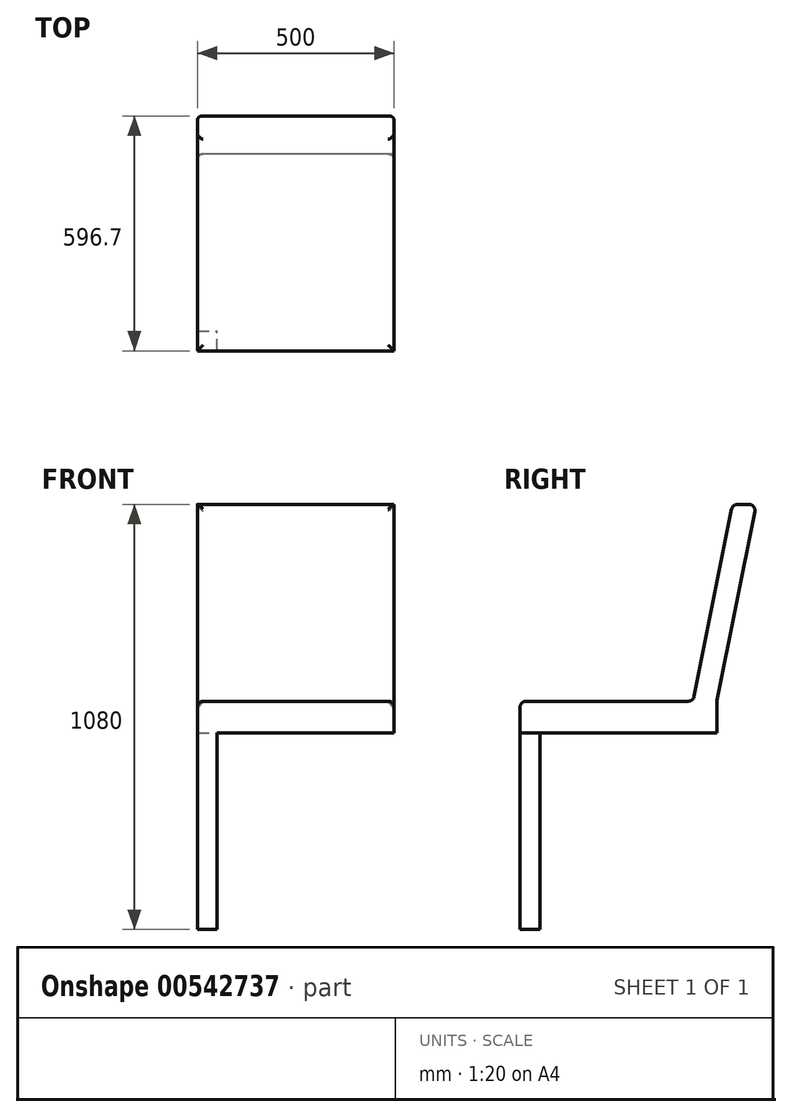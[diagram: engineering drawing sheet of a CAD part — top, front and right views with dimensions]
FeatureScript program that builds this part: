
annotation { "Feature Type Name" : "Feature", "Feature Type Description" : "" }
export const myFeature = defineFeature(function(context is Context, id is Id, definition is map)
    precondition{}
    {
        {
            var Q0;
            Q0=qCreatedBy(makeId("Top.planeOp"),FACE);
            var sketch = newSketch(context, id + "F0", { "sketchPlane" : qUnion([Q0])});
            skLineSegment(sketch, "E0.bottom", {"start": v(250, 250) * mm, "end": v(-250, 250) * mm});
            skLineSegment(sketch, "E0.top", {"start": v(250, -250) * mm, "end": v(-250, -250) * mm});
            skLineSegment(sketch, "E0.left", {"start": v(250, 250) * mm, "end": v(250, -250) * mm});
            skLineSegment(sketch, "E0.right", {"start": v(-250, 250) * mm, "end": v(-250, -250) * mm});
            skPoint(sketch, "E0.middle", {"position": v(0, 0) * mm});
            skSolve(sketch);
        }
        {
            var Q0;
            Q0 = qSketchRegion(id + "F0", true);
            extrude(context, id + "F1", {"entities" : qUnion([Q0]), "depth" : 80 * mm, "offsetDistance" : 25 * mm});
        }
        {
            var Q0;
            Q0=makeQuery(id+"F1.opExtrude","CAP_FACE",FACE,{"disambiguationData":[OSD([sQuery(id+"F0.wireOp",EDGE,"E0.bottom"),sQuery(id+"F0.wireOp",EDGE,"E0.top"),sQuery(id+"F0.wireOp",EDGE,"E0.left"),sQuery(id+"F0.wireOp",EDGE,"E0.right")])],"isStart":true});
            var sketch = newSketch(context, id + "F2", { "sketchPlane" : qUnion([Q0])});
            skLineSegment(sketch, "E1.bottom", {"start": v(-250, 250) * mm, "end": v(-200, 250) * mm});
            skLineSegment(sketch, "E1.top", {"start": v(-250, 200) * mm, "end": v(-200, 200) * mm});
            skLineSegment(sketch, "E1.left", {"start": v(-250, 250) * mm, "end": v(-250, 200) * mm});
            skLineSegment(sketch, "E1.right", {"start": v(-200, 250) * mm, "end": v(-200, 200) * mm});
            skSolve(sketch);
        }
        {
            var Q0;
            Q0 = qSketchRegion(id + "F2", true);
            extrude(context, id + "F3", {"entities" : qUnion([Q0]), "operationType" : NewBodyOperationType.ADD, "depth" : 500 * mm, "offsetDistance" : 25 * mm});
        }
        {
            var Q0;
            Q0=qCreatedBy(makeId("Front.planeOp"),FACE);
            var sketch = newSketch(context, id + "F4", { "sketchPlane" : qUnion([Q0])});
            skLineSegment(sketch, "E2", {"start": v(0, 0) * mm, "end": v(0, -54.17) * mm});
            skSolve(sketch);
        }
        {
            var Q0;
            Q0=qCreatedBy(makeId("Right.planeOp"),FACE);
            var sketch = newSketch(context, id + "F5", { "sketchPlane" : qUnion([Q0])});
            skLineSegment(sketch, "E3", {"start": v(190, 80) * mm, "end": v(290, 580) * mm});
            skLineSegment(sketch, "E4", {"start": v(290, 580) * mm, "end": v(350, 580) * mm});
            skLineSegment(sketch, "E5", {"start": v(350, 580) * mm, "end": v(250, 80) * mm});
            skLineSegment(sketch, "E6", {"start": v(250, 80) * mm, "end": v(190, 80) * mm});
            skSolve(sketch);
        }
        {
            var Q0;
            Q0 = qSketchRegion(id + "F5", true);
            extrude(context, id + "F6", {"entities" : qUnion([Q0]), "operationType" : NewBodyOperationType.ADD, "depth" : 500 * mm, "offsetDistance" : 25 * mm, "symmetric" : true});
        }
        {
            var Q0;
            Q0=makeQuery(id+"F1.opExtrude","CAP_FACE",FACE,{"disambiguationData":[OSD([sQuery(id+"F0.wireOp",EDGE,"E0.bottom"),sQuery(id+"F0.wireOp",EDGE,"E0.top"),sQuery(id+"F0.wireOp",EDGE,"E0.left"),sQuery(id+"F0.wireOp",EDGE,"E0.right")])],"isStart":false});
            var Q1;
            Q1=makeQuery(id+"F6.opExtrude","SWEPT_FACE",FACE,{"disambiguationData":[OSD([sQuery(id+"F5.wireOp",EDGE,"E3")])]});
            var Q2;
            Q2=makeQuery(id+"F6.opExtrude","SWEPT_FACE",FACE,{"disambiguationData":[OSD([sQuery(id+"F5.wireOp",EDGE,"E5")])]});
            fillet(context, id + "F7", {"entities" : qUnion([Q0, Q1, Q2]), "radius" : 15 * mm, "tangentPropagation" : true, "allowEdgeOverflow" : false});
        }
    });
